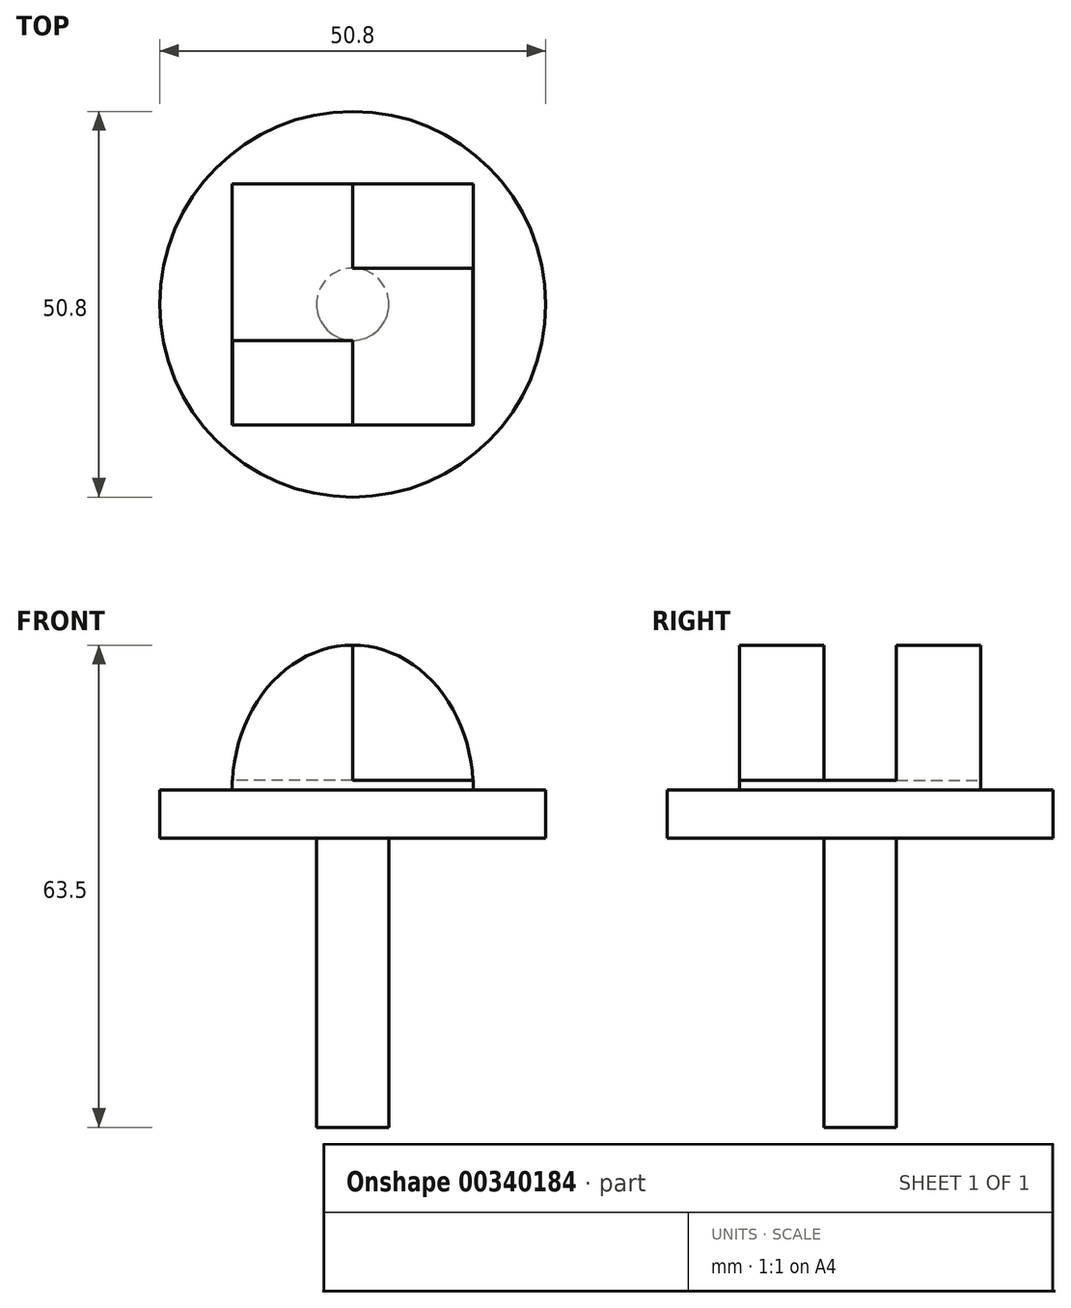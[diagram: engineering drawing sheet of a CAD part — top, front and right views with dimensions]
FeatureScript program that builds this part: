
annotation { "Feature Type Name" : "Feature", "Feature Type Description" : "" }
export const myFeature = defineFeature(function(context is Context, id is Id, definition is map)
    precondition{}
    {
        {
            var Q0;
            Q0=qCreatedBy(makeId("Front.planeOp"),FACE);
            var sketch = newSketch(context, id + "F0", { "sketchPlane" : qUnion([Q0])});
            skLineSegment(sketch, "E0", {"start": v(0, 0) * mm, "end": v(0, 0) * mm});
            skLineSegment(sketch, "E1", {"start": v(0, 0) * mm, "end": v(-4.76, 0) * mm});
            skLineSegment(sketch, "E2", {"start": v(-4.76, -6.35) * mm, "end": v(-4.76, 0) * mm});
            skLineSegment(sketch, "E3", {"start": v(-4.76, -6.35) * mm, "end": v(-25.4, -6.35) * mm});
            skLineSegment(sketch, "E4", {"start": v(-25.4, -6.35) * mm, "end": v(-25.4, 0) * mm});
            skLineSegment(sketch, "E5", {"start": v(-25.4, 0) * mm, "end": v(0, 0) * mm});
            skLineSegment(sketch, "E6", {"start": v(0, 0) * mm, "end": v(0, -6.35) * mm});
            skSolve(sketch);
        }
        {
            var Q0;
            {var subQ0=sQuery(id+"F0.wireOp",EDGE,"E2");Q0=makeQuery(id+"F0.imprint","IMPRINT",FACE,{"disambiguationData":[TD([[makeQuery(id+"F0.imprint","IMPRINT",EDGE,{"derivedFrom":subQ0}),1.0]])]});}
            var Q1;
            Q1=sQuery(id+"F0.wireOp",EDGE,"E6");
            revolve(context, id + "F1", {"entities" : qUnion([Q0]), "axis" : qUnion([Q1]), "revolveType" : RevolveType.FULL});
        }
        {
            var Q0;
            Q0=makeQuery(id+"F1.opRevolve","SWEPT_FACE",FACE,{"disambiguationData":[OSD([sQuery(id+"F0.wireOp",EDGE,"E5")])]});
            var sketch = newSketch(context, id + "F2", { "sketchPlane" : qUnion([Q0])});
            skLineSegment(sketch, "E7.bottom", {"start": v(15.88, -15.87) * mm, "end": v(-15.87, -15.88) * mm});
            skLineSegment(sketch, "E7.top", {"start": v(15.87, 15.88) * mm, "end": v(-15.88, 15.88) * mm});
            skLineSegment(sketch, "E7.left", {"start": v(15.88, -15.87) * mm, "end": v(15.87, 15.88) * mm});
            skLineSegment(sketch, "E7.right", {"start": v(-15.88, -15.88) * mm, "end": v(-15.88, 15.88) * mm});
            skPoint(sketch, "E7.middle", {"position": v(0, 0) * mm});
            skCircle(sketch, "E8.0", {"center": v(0, 0) * mm, "radius": 4.76 * mm});
            skSolve(sketch);
        }
        {
            var Q0;
            Q0 = qSketchRegion(id + "F2", true);
            extrude(context, id + "F3", {"entities" : qUnion([Q0]), "operationType" : NewBodyOperationType.ADD, "depth" : 19.05 * mm});
        }
        {
            var Q0;
            Q0=makeQuery(id+"F3.opExtrude","SWEPT_FACE",FACE,{"disambiguationData":[OSD([sQuery(id+"F2.wireOp",EDGE,"E7.left")])]});
            var sketch = newSketch(context, id + "F4", { "sketchPlane" : qUnion([Q0])});
            skLineSegment(sketch, "E9", {"start": v(0, 19.05) * mm, "end": v(0, 0) * mm});
            skCircle(sketch, "E10", {"center": v(0, 6.35) * mm, "radius": 4.76 * mm});
            skLineSegment(sketch, "E11", {"start": v(-4.76, 6.35) * mm, "end": v(-4.76, 19.05) * mm});
            skLineSegment(sketch, "E12", {"start": v(4.76, 6.35) * mm, "end": v(4.76, 19.05) * mm});
            skSolve(sketch);
        }
        {
            var Q0;
            {var subQ5=sQuery(id+"F4.wireOp",EDGE,"E11");Q0=makeQuery(id+"F4.imprint","IMPRINT",FACE,{"disambiguationData":[TD([[makeQuery(id+"F4.imprint","IMPRINT",EDGE,{"derivedFrom":subQ5}),-1.0]])]});}
            var Q1;
            {var subQ0=sQuery(id+"F4.wireOp",EDGE,"E10");var subQ1=sQuery(id+"F4.wireOp",EDGE,"E9");var subQ2=makeQuery(id+"F4.imprint","INTERSECT",VERTEX,{"disambiguationData":[OD(0.0)],"derivedFrom":[subQ1,subQ0]});Q1=makeQuery(id+"F4.imprint","IMPRINT",FACE,{"disambiguationData":[TD([[makeQuery(id+"F4.imprint","IMPRINT",EDGE,{"disambiguationData":[TD([[subQ2,-1.0]])],"derivedFrom":subQ1}),1.0]])]});}
            var Q2;
            {var subQ0=sQuery(id+"F4.wireOp",EDGE,"E10");var subQ1=sQuery(id+"F4.wireOp",EDGE,"E9");var subQ2=makeQuery(id+"F4.imprint","INTERSECT",VERTEX,{"disambiguationData":[OD(0.0)],"derivedFrom":[subQ1,subQ0]});Q2=makeQuery(id+"F4.imprint","IMPRINT",FACE,{"disambiguationData":[TD([[makeQuery(id+"F4.imprint","IMPRINT",EDGE,{"disambiguationData":[TD([[subQ2,-1.0]])],"derivedFrom":subQ1}),-1.0]])]});}
            var Q3;
            {var subQ5=sQuery(id+"F4.wireOp",EDGE,"E12");Q3=makeQuery(id+"F4.imprint","IMPRINT",FACE,{"disambiguationData":[TD([[makeQuery(id+"F4.imprint","IMPRINT",EDGE,{"derivedFrom":subQ5}),1.0]])]});}
            extrude(context, id + "F5", {"entities" : qUnion([Q0, Q1, Q2, Q3]), "operationType" : NewBodyOperationType.REMOVE, "endBound" : BoundingType.THROUGH_ALL, "oppositeDirection" : true, "depth" : 25.4 * mm});
        }
        {
            var Q0;
            Q0=makeQuery(id+"F3.opExtrude","SWEPT_FACE",FACE,{"disambiguationData":[OSD([sQuery(id+"F2.wireOp",EDGE,"E7.bottom")])]});
            var sketch = newSketch(context, id + "F6", { "sketchPlane" : qUnion([Q0])});
            skLineSegment(sketch, "E13.0.0", {"start": v(-15.88, 0) * mm, "end": v(15.88, 0) * mm});
            skLineSegment(sketch, "E13.0.1", {"start": v(15.88, 0) * mm, "end": v(15.88, 19.05) * mm});
            skLineSegment(sketch, "E13.0.2", {"start": v(15.88, 19.05) * mm, "end": v(-15.88, 19.05) * mm});
            skLineSegment(sketch, "E13.0.3", {"start": v(-15.88, 19.05) * mm, "end": v(-15.88, 0) * mm});
            skLineSegment(sketch, "E14", {"start": v(0, 19.05) * mm, "end": v(0, 0) * mm});
            skCircle(sketch, "E15", {"center": v(0, 9.53) * mm, "radius": 6.35 * mm});
            skSolve(sketch);
        }
        {
            var Q0;
            {var subQ0=sQuery(id+"F6.wireOp",EDGE,"E15");var subQ1=sQuery(id+"F6.wireOp",EDGE,"E14");var subQ2=makeQuery(id+"F6.imprint","INTERSECT",VERTEX,{"disambiguationData":[OD(0.0)],"derivedFrom":[subQ1,subQ0]});Q0=makeQuery(id+"F6.imprint","IMPRINT",FACE,{"disambiguationData":[TD([[makeQuery(id+"F6.imprint","IMPRINT",EDGE,{"disambiguationData":[TD([[subQ2,-1.0]])],"derivedFrom":subQ1}),1.0]])]});}
            var Q1;
            {var subQ0=sQuery(id+"F6.wireOp",EDGE,"E15");var subQ1=sQuery(id+"F6.wireOp",EDGE,"E14");var subQ2=makeQuery(id+"F6.imprint","INTERSECT",VERTEX,{"disambiguationData":[OD(0.0)],"derivedFrom":[subQ1,subQ0]});Q1=makeQuery(id+"F6.imprint","IMPRINT",FACE,{"disambiguationData":[TD([[makeQuery(id+"F6.imprint","IMPRINT",EDGE,{"disambiguationData":[TD([[subQ2,-1.0]])],"derivedFrom":subQ1}),-1.0]])]});}
            extrude(context, id + "F7", {"entities" : qUnion([Q0, Q1]), "operationType" : NewBodyOperationType.REMOVE, "endBound" : BoundingType.THROUGH_ALL, "oppositeDirection" : true, "depth" : 25.4 * mm});
        }
        {
            var Q0;
            {var subQ0=sQuery(id+"F2.wireOp",EDGE,"E7.bottom");var subQ1=sQuery(id+"F2.wireOp",EDGE,"E7.right");var subQ2=sQuery(id+"F2.wireOp",EDGE,"E7.left");Q0=makeQuery(id+"F5.boolean.opBoolean","SPLIT",FACE,{"disambiguationData":[TD([makeQuery(id+"F3.opExtrude","SWEPT_FACE",FACE,{"disambiguationData":[OSD([subQ0])]})])],"derivedFrom":makeQuery(id+"F3.opExtrude","CAP_FACE",FACE,{"disambiguationData":[OSD([subQ0,sQuery(id+"F2.wireOp",EDGE,"E7.top"),subQ2,subQ1,sQuery(id+"F2.wireOp",EDGE,"E8.0")])],"isStart":false})});}
            var sketch = newSketch(context, id + "F8", { "sketchPlane" : qUnion([Q0])});
            skLineSegment(sketch, "E16.0", {"start": v(15.88, -15.87) * mm, "end": v(-15.87, -15.88) * mm});
            skLineSegment(sketch, "E17.0", {"start": v(15.88, -15.87) * mm, "end": v(15.87, 15.88) * mm});
            skLineSegment(sketch, "E18.0", {"start": v(15.87, 15.88) * mm, "end": v(-15.88, 15.88) * mm});
            skLineSegment(sketch, "E19.0", {"start": v(-15.88, -15.88) * mm, "end": v(-15.88, 15.88) * mm});
            skLineSegment(sketch, "E20", {"start": v(-15.88, 0) * mm, "end": v(15.88, 0) * mm});
            skLineSegment(sketch, "E21", {"start": v(0, -15.88) * mm, "end": v(0, 15.88) * mm});
            skSolve(sketch);
        }
        {
            var Q0;
            {var subQ0=sQuery(id+"F8.wireOp",EDGE,"E17.0");var subQ1=sQuery(id+"F8.wireOp",EDGE,"E16.0");var subQ2=makeQuery(id+"F8.imprint","INTERSECT",VERTEX,{"derivedFrom":[subQ1,subQ0]});Q0=makeQuery(id+"F8.imprint","IMPRINT",FACE,{"disambiguationData":[TD([[makeQuery(id+"F8.imprint","IMPRINT",EDGE,{"disambiguationData":[TD([[subQ2,-1.0]])],"derivedFrom":subQ1}),-1.0]])]});}
            var Q1;
            {var subQ0=sQuery(id+"F8.wireOp",EDGE,"E17.0");var subQ3=sQuery(id+"F8.wireOp",EDGE,"E20");var subQ4=makeQuery(id+"F8.imprint","INTERSECT",VERTEX,{"derivedFrom":[subQ0,subQ3]});Q1=makeQuery(id+"F8.imprint","IMPRINT",FACE,{"disambiguationData":[TD([[makeQuery(id+"F8.imprint","IMPRINT",EDGE,{"disambiguationData":[TD([[subQ4,1.0]])],"derivedFrom":subQ3}),-1.0]])]});}
            var Q2;
            {var subQ0=sQuery(id+"F8.wireOp",EDGE,"E19.0");var subQ1=sQuery(id+"F8.wireOp",EDGE,"E18.0");var subQ2=makeQuery(id+"F8.imprint","INTERSECT",VERTEX,{"derivedFrom":[subQ1,subQ0]});Q2=makeQuery(id+"F8.imprint","IMPRINT",FACE,{"disambiguationData":[TD([[makeQuery(id+"F8.imprint","IMPRINT",EDGE,{"disambiguationData":[TD([[subQ2,1.0]])],"derivedFrom":subQ1}),1.0]])]});}
            extrude(context, id + "F9", {"entities" : qUnion([Q0, Q1, Q2]), "operationType" : NewBodyOperationType.REMOVE, "oppositeDirection" : true, "depth" : 17.78 * mm});
        }
        {
            var Q0;
            Q0=makeQuery(id+"F3.opExtrude","SWEPT_FACE",FACE,{"disambiguationData":[OSD([sQuery(id+"F2.wireOp",EDGE,"E7.top")])]});
            var sketch = newSketch(context, id + "F10", { "sketchPlane" : qUnion([Q0])});
            skLineSegment(sketch, "E22.0", {"start": v(-15.87, 19.05) * mm, "end": v(-15.87, 0) * mm});
            skLineSegment(sketch, "E23.0", {"start": v(15.87, 19.05) * mm, "end": v(15.87, 0) * mm});
            skLineSegment(sketch, "E24", {"start": v(-15.87, 0) * mm, "end": v(15.87, 0) * mm});
            skEllipse(sketch, "E25", {"center": v(0, 0) * mm, "majorRadius": 19.05 * mm, "minorRadius": 15.87 * mm, "majorAxis": v(0, 1)});
            skLineSegment(sketch, "E26.0", {"start": v(-15.87, 19.05) * mm, "end": v(0, 19.05) * mm});
            skLineSegment(sketch, "E27.0", {"start": v(15.88, 19.05) * mm, "end": v(0, 19.05) * mm});
            skSolve(sketch);
        }
        {
            var Q0;
            {var subQ0=sQuery(id+"F10.wireOp",EDGE,"E22.0");Q0=makeQuery(id+"F10.imprint","IMPRINT",FACE,{"disambiguationData":[TD([[makeQuery(id+"F10.imprint","IMPRINT",EDGE,{"derivedFrom":subQ0}),1.0]])]});}
            var Q1;
            {var subQ4=sQuery(id+"F10.wireOp",EDGE,"E27.0");Q1=makeQuery(id+"F10.imprint","IMPRINT",FACE,{"disambiguationData":[TD([[makeQuery(id+"F10.imprint","IMPRINT",EDGE,{"derivedFrom":subQ4}),1.0]])]});}
            extrude(context, id + "F11", {"entities" : qUnion([Q0, Q1]), "operationType" : NewBodyOperationType.REMOVE, "endBound" : BoundingType.THROUGH_ALL, "oppositeDirection" : true, "depth" : 25.4 * mm});
        }
        {
            var Q0;
            Q0=makeQuery(id+"F3.opExtrude","SWEPT_FACE",FACE,{"disambiguationData":[OSD([sQuery(id+"F2.wireOp",EDGE,"E7.top")])]});
            var sketch = newSketch(context, id + "F12", { "sketchPlane" : qUnion([Q0])});
            skCircle(sketch, "E28", {"center": v(0, 9.53) * mm, "radius": 4.76 * mm});
            skSolve(sketch);
        }
        {
            var Q0;
            Q0 = qSketchRegion(id + "F12", true);
            var Q1;
            Q1=makeQuery(id+"F3.opExtrude","SWEPT_FACE",FACE,{"disambiguationData":[OSD([sQuery(id+"F2.wireOp",EDGE,"E7.bottom")])]});
            extrude(context, id + "F13", {"entities" : qUnion([Q0]), "endBound" : BoundingType.UP_TO_SURFACE, "oppositeDirection" : true, "endBoundEntityFace" : qUnion([Q1]), "depth" : 25.4 * mm});
        }
        {
            var Q0;
            Q0=makeQuery(id+"F3.opExtrude","SWEPT_FACE",FACE,{"disambiguationData":[OSD([sQuery(id+"F2.wireOp",EDGE,"E7.top")])]});
            var sketch = newSketch(context, id + "F14", { "sketchPlane" : qUnion([Q0])});
            skCircle(sketch, "E29.0.0", {"center": v(0, 9.53) * mm, "radius": 4.76 * mm});
            skArc(sketch, "E30.0", {"start": v(0, 3.17) * mm, "mid": v(-6.35, 9.53) * mm, "end": v(0, 15.88) * mm});
            skArc(sketch, "E31.0", {"start": v(0, 15.88) * mm, "mid": v(6.35, 9.53) * mm, "end": v(0, 3.17) * mm});
            skCircle(sketch, "E32", {"center": v(-14.29, 9.52) * mm, "radius": 9.53 * mm});
            skLineSegment(sketch, "E33", {"start": v(-14.29, 9.52) * mm, "end": v(-4.76, 9.52) * mm});
            skCircle(sketch, "E34", {"center": v(14.29, 9.53) * mm, "radius": 9.53 * mm});
            skLineSegment(sketch, "E35", {"start": v(0, 15.88) * mm, "end": v(0, 3.17) * mm});
            skSolve(sketch);
        }
        {
            var Q0;
            {var subQ1=sQuery(id+"F14.wireOp",EDGE,"E29.0.0");var subQ3=sQuery(id+"F14.wireOp",EDGE,"E35");var subQ4=makeQuery(id+"F14.imprint","INTERSECT",VERTEX,{"disambiguationData":[OD(0.0)],"derivedFrom":[subQ1,subQ3]});Q0=makeQuery(id+"F14.imprint","IMPRINT",FACE,{"disambiguationData":[TD([[makeQuery(id+"F14.imprint","IMPRINT",EDGE,{"disambiguationData":[TD([[subQ4,-1.0]])],"derivedFrom":subQ1}),-1.0]])]});}
            var Q1;
            {var subQ0=sQuery(id+"F14.wireOp",EDGE,"E33");var subQ1=sQuery(id+"F14.wireOp",EDGE,"E30.0");var subQ2=makeQuery(id+"F14.imprint","INTERSECT",VERTEX,{"derivedFrom":[subQ1,subQ0]});Q1=makeQuery(id+"F14.imprint","IMPRINT",FACE,{"disambiguationData":[TD([[makeQuery(id+"F14.imprint","IMPRINT",EDGE,{"disambiguationData":[TD([[subQ2,-1.0]])],"derivedFrom":subQ1}),-1.0]])]});}
            var Q2;
            {var subQ0=sQuery(id+"F14.wireOp",EDGE,"E32");var subQ1=sQuery(id+"F14.wireOp",EDGE,"E30.0");var subQ2=makeQuery(id+"F14.imprint","INTERSECT",VERTEX,{"disambiguationData":[OD(0.0)],"derivedFrom":[subQ1,subQ0]});Q2=makeQuery(id+"F14.imprint","IMPRINT",FACE,{"disambiguationData":[TD([[makeQuery(id+"F14.imprint","IMPRINT",EDGE,{"disambiguationData":[TD([[subQ2,-1.0]])],"derivedFrom":subQ1}),-1.0]])]});}
            var Q3;
            {var subQ1=sQuery(id+"F14.wireOp",EDGE,"E29.0.0");var subQ3=sQuery(id+"F14.wireOp",EDGE,"E35");var subQ4=makeQuery(id+"F14.imprint","INTERSECT",VERTEX,{"disambiguationData":[OD(1.0)],"derivedFrom":[subQ1,subQ3]});Q3=makeQuery(id+"F14.imprint","IMPRINT",FACE,{"disambiguationData":[TD([[makeQuery(id+"F14.imprint","IMPRINT",EDGE,{"disambiguationData":[TD([[subQ4,1.0]])],"derivedFrom":subQ1}),-1.0]])]});}
            var Q4;
            Q4=makeQuery(id+"F5.boolean.opBoolean","COPY",FACE,{"derivedFrom":makeQuery(id+"F5.opExtrude","SWEPT_FACE",FACE,{"disambiguationData":[OSD([sQuery(id+"F4.wireOp",EDGE,"E12")])]})});
            extrude(context, id + "F15", {"entities" : qUnion([Q0, Q1, Q2, Q3]), "operationType" : NewBodyOperationType.ADD, "endBound" : BoundingType.UP_TO_SURFACE, "oppositeDirection" : true, "endBoundEntityFace" : qUnion([Q4]), "depth" : 25.4 * mm});
        }
        {
            var Q0;
            Q0=makeQuery(id+"F3.opExtrude","SWEPT_FACE",FACE,{"disambiguationData":[OSD([sQuery(id+"F2.wireOp",EDGE,"E7.bottom")])]});
            var sketch = newSketch(context, id + "F16", { "sketchPlane" : qUnion([Q0])});
            skCircle(sketch, "E36.0.0", {"center": v(0, 9.53) * mm, "radius": 4.76 * mm});
            skArc(sketch, "E37.0", {"start": v(0, 15.88) * mm, "mid": v(-6.35, 9.53) * mm, "end": v(0, 3.17) * mm});
            skLineSegment(sketch, "E38", {"start": v(0, 15.88) * mm, "end": v(0, 3.17) * mm});
            skSolve(sketch);
        }
        {
            var Q0;
            {var subQ4=sQuery(id+"F16.wireOp",EDGE,"E37.0");Q0=makeQuery(id+"F16.imprint","IMPRINT",FACE,{"disambiguationData":[TD([[makeQuery(id+"F16.imprint","IMPRINT",EDGE,{"derivedFrom":subQ4}),1.0]])]});}
            var Q1;
            Q1=makeQuery(id+"F5.boolean.opBoolean","COPY",FACE,{"derivedFrom":makeQuery(id+"F5.opExtrude","SWEPT_FACE",FACE,{"disambiguationData":[OSD([sQuery(id+"F4.wireOp",EDGE,"E11")])]})});
            extrude(context, id + "F17", {"entities" : qUnion([Q0]), "operationType" : NewBodyOperationType.ADD, "endBound" : BoundingType.UP_TO_SURFACE, "oppositeDirection" : true, "endBoundEntityFace" : qUnion([Q1]), "depth" : 25.4 * mm});
        }
        {
            var Q0;
            {var subQ11=sQuery(id+"F14.wireOp",EDGE,"E32");var subQ12=sQuery(id+"F14.wireOp",EDGE,"E30.0");var subQ13=makeQuery(id+"F14.imprint","INTERSECT",VERTEX,{"disambiguationData":[OD(0.0)],"derivedFrom":[subQ12,subQ11]});Q0=makeQuery(id+"F14.imprint","IMPRINT",FACE,{"disambiguationData":[TD([[makeQuery(id+"F14.imprint","IMPRINT",EDGE,{"disambiguationData":[TD([[subQ13,1.0]])],"derivedFrom":subQ11}),-1.0]])]});}
            var Q1;
            {var subQ0=sQuery(id+"F14.wireOp",EDGE,"E31.0");var subQ11=sQuery(id+"F14.wireOp",EDGE,"E34");var subQ12=makeQuery(id+"F14.imprint","INTERSECT",VERTEX,{"disambiguationData":[OD(1.0)],"derivedFrom":[subQ0,subQ11]});Q1=makeQuery(id+"F14.imprint","IMPRINT",FACE,{"disambiguationData":[TD([[makeQuery(id+"F14.imprint","IMPRINT",EDGE,{"disambiguationData":[TD([[subQ12,-1.0]])],"derivedFrom":subQ11}),-1.0]])]});}
            var Q2;
            {var subQ1=sQuery(id+"F14.wireOp",EDGE,"E29.0.0");var subQ16=sQuery(id+"F14.wireOp",EDGE,"E34");var subQ18=makeQuery(id+"F14.imprint","INTERSECT",VERTEX,{"derivedFrom":[subQ1,subQ16]});Q2=makeQuery(id+"F14.imprint","IMPRINT",FACE,{"disambiguationData":[TD([[makeQuery(id+"F14.imprint","IMPRINT",EDGE,{"disambiguationData":[TD([[subQ18,-1.0]])],"derivedFrom":subQ16}),-1.0]])]});}
            var Q3;
            {var subQ1=sQuery(id+"F14.wireOp",EDGE,"E29.0.0");var subQ3=sQuery(id+"F14.wireOp",EDGE,"E35");var subQ4=makeQuery(id+"F14.imprint","INTERSECT",VERTEX,{"disambiguationData":[OD(1.0)],"derivedFrom":[subQ1,subQ3]});Q3=makeQuery(id+"F14.imprint","IMPRINT",FACE,{"disambiguationData":[TD([[makeQuery(id+"F14.imprint","IMPRINT",EDGE,{"disambiguationData":[TD([[subQ4,1.0]])],"derivedFrom":subQ1}),-1.0]])]});}
            var Q4;
            Q4=makeQuery(id+"F3.opExtrude","SWEPT_FACE",FACE,{"disambiguationData":[OSD([sQuery(id+"F2.wireOp",EDGE,"E7.bottom")])]});
            extrude(context, id + "F18", {"entities" : qUnion([Q0, Q1, Q2, Q3]), "endBound" : BoundingType.UP_TO_SURFACE, "oppositeDirection" : true, "endBoundEntityFace" : qUnion([Q4]), "depth" : 25.4 * mm});
        }
        {
            var Q0;
            Q0=makeQuery(id+"F1.opRevolve","SWEPT_BODY",BODY,{"disambiguationData":[OSD([sQuery(id+"F0.wireOp",EDGE,"E2"),sQuery(id+"F0.wireOp",EDGE,"E3"),sQuery(id+"F0.wireOp",EDGE,"E4"),sQuery(id+"F0.wireOp",EDGE,"E5")])]});
            var Q1;
            Q1=makeQuery(id+"F18.opExtrude","SWEPT_BODY",BODY,{"disambiguationData":[OSD([sQuery(id+"F2.wireOp",EDGE,"E7.top"),sQuery(id+"F14.wireOp",EDGE,"E29.0.0"),sQuery(id+"F14.wireOp",EDGE,"E32"),sQuery(id+"F14.wireOp",EDGE,"E34")])]});
            booleanBodies(context, id + "F19", {"operationType" : BooleanOperationType.UNION, "tools" : qUnion([Q0, Q1])});
        }
        {
            var Q0;
            Q0=makeQuery(id+"F9.boolean.opBoolean","COPY",FACE,{"derivedFrom":makeQuery(id+"F9.opExtrude","CAP_FACE",FACE,{"disambiguationData":[OSD([sQuery(id+"F8.wireOp",EDGE,"E16.0"),sQuery(id+"F8.wireOp",EDGE,"E17.0"),sQuery(id+"F8.wireOp",EDGE,"E20"),sQuery(id+"F8.wireOp",EDGE,"E21")])],"isStart":false})});
            var sketch = newSketch(context, id + "F20", { "sketchPlane" : qUnion([Q0])});
            skLineSegment(sketch, "E39.0", {"start": v(-15.88, -15.88) * mm, "end": v(-15.88, 15.88) * mm});
            skLineSegment(sketch, "E40.0", {"start": v(15.88, -15.87) * mm, "end": v(15.87, 15.88) * mm});
            skLineSegment(sketch, "E41", {"start": v(-15.87, -15.87) * mm, "end": v(15.88, 15.88) * mm, "construction": true});
            skLineSegment(sketch, "E42.bottom", {"start": v(15.88, 4.76) * mm, "end": v(-15.87, 4.76) * mm});
            skLineSegment(sketch, "E42.top", {"start": v(15.88, -4.76) * mm, "end": v(-15.87, -4.76) * mm});
            skLineSegment(sketch, "E42.left", {"start": v(15.88, 4.76) * mm, "end": v(15.88, -4.76) * mm});
            skLineSegment(sketch, "E42.right", {"start": v(-15.87, 4.76) * mm, "end": v(-15.87, -4.76) * mm});
            skPoint(sketch, "E42.middle", {"position": v(0, 0) * mm});
            skSolve(sketch);
        }
        {
            var Q0;
            Q0=makeQuery(id+"F20.imprint","IMPRINT",FACE,{"disambiguationData":[TD([[makeQuery(id+"F20.imprint","IMPRINT",EDGE,{"derivedFrom":sQuery(id+"F20.wireOp",EDGE,"E42.bottom")}),1.0]])]});
            var Q1;
            {var subQ14=sQuery(id+"F8.wireOp",EDGE,"E20");var subQ16=sQuery(id+"F8.wireOp",EDGE,"E17.0");var subQ22=makeQuery(id+"F9.boolean.opBoolean","COPY",EDGE,{"derivedFrom":makeQuery(id+"F9.opExtrude","CAP_EDGE",EDGE,{"disambiguationData":[OSD([subQ14]),TDD([makeQuery(id+"F8.imprint","IMPRINT",EDGE,{"disambiguationData":[TD([[makeQuery(id+"F8.imprint","INTERSECT",VERTEX,{"derivedFrom":[subQ16,subQ14]}),1.0]])],"derivedFrom":subQ14})])],"isStart":false})});Q1=makeQuery(id+"F20.imprint","IMPRINT",FACE,{"disambiguationData":[TD([[makeQuery(id+"F20.imprint","IMPRINT",EDGE,{"derivedFrom":subQ22}),-1.0]])]});}
            extrude(context, id + "F21", {"entities" : qUnion([Q0, Q1]), "operationType" : NewBodyOperationType.REMOVE, "depth" : 25.4 * mm});
        }
        {
            var Q0;
            {var subQ0=sQuery(id+"F8.wireOp",EDGE,"E21");var subQ1=sQuery(id+"F8.wireOp",EDGE,"E20");var subQ2=sQuery(id+"F8.wireOp",EDGE,"E18.0");Q0=makeQuery(id+"F21.boolean.opBoolean","MERGE",FACE,{"derivedFrom":[makeQuery(id+"F11.boolean.opBoolean","MERGE",FACE,{"derivedFrom":[makeQuery(id+"F9.boolean.opBoolean","COPY",FACE,{"derivedFrom":makeQuery(id+"F9.opExtrude","CAP_FACE",FACE,{"disambiguationData":[OSD([subQ2,sQuery(id+"F8.wireOp",EDGE,"E19.0"),subQ1,subQ0])],"isStart":false})}),makeQuery(id+"F11.opExtrude","SWEPT_FACE",FACE,{"disambiguationData":[OSD([subQ2])]})]}),makeQuery(id+"F9.boolean.opBoolean","COPY",FACE,{"derivedFrom":makeQuery(id+"F9.opExtrude","CAP_FACE",FACE,{"disambiguationData":[OSD([sQuery(id+"F8.wireOp",EDGE,"E16.0"),sQuery(id+"F8.wireOp",EDGE,"E17.0"),subQ1,subQ0])],"isStart":false})}),makeQuery(id+"F21.opExtrude","CAP_FACE",FACE,{"disambiguationData":[OSD([sQuery(id+"F20.wireOp",EDGE,"E42.bottom"),sQuery(id+"F20.wireOp",EDGE,"E42.top"),sQuery(id+"F20.wireOp",EDGE,"E42.left"),sQuery(id+"F20.wireOp",EDGE,"E42.right")])],"isStart":true})]});}
            var sketch = newSketch(context, id + "F22", { "sketchPlane" : qUnion([Q0])});
            skLineSegment(sketch, "E43.bottom", {"start": v(15.84, -15.88) * mm, "end": v(-15.84, -15.88) * mm});
            skLineSegment(sketch, "E43.top", {"start": v(0, 15.88) * mm, "end": v(-15.84, 15.88) * mm});
            skLineSegment(sketch, "E43.left", {"start": v(15.84, -15.88) * mm, "end": v(15.84, 15.88) * mm});
            skLineSegment(sketch, "E43.right", {"start": v(-15.84, 4.76) * mm, "end": v(-15.84, 15.88) * mm});
            skPoint(sketch, "E43.middle", {"position": v(0, 0) * mm});
            skLineSegment(sketch, "E44.0", {"start": v(0, 4.76) * mm, "end": v(0, 15.88) * mm});
            skLineSegment(sketch, "E45.0", {"start": v(0, -15.88) * mm, "end": v(0, -4.76) * mm});
            skLineSegment(sketch, "E46", {"start": v(0, -4.76) * mm, "end": v(15.84, -4.76) * mm});
            skLineSegment(sketch, "E47", {"start": v(0, 4.76) * mm, "end": v(-15.84, 4.76) * mm});
            skSolve(sketch);
        }
        {
            var Q0;
            Q0 = qSketchRegion(id + "F22", true);
            extrude(context, id + "F23", {"entities" : qUnion([Q0]), "operationType" : NewBodyOperationType.REMOVE, "depth" : 25.4 * mm});
        }
        {
            var Q0;
            Q0=makeQuery(id+"F18.opExtrude","SWEPT_FACE",FACE,{"disambiguationData":[OSD([sQuery(id+"F2.wireOp",EDGE,"E7.top")])]});
            var sketch = newSketch(context, id + "F24", { "sketchPlane" : qUnion([Q0])});
            skCircle(sketch, "E48.0.0", {"center": v(0, 0) * mm, "radius": 4.76 * mm});
            skSolve(sketch);
        }
        {
            var Q0;
            Q0 = qSketchRegion(id + "F24", true);
            extrude(context, id + "F25", {"entities" : qUnion([Q0]), "operationType" : NewBodyOperationType.ADD, "depth" : 44.45 * mm});
        }
    });
